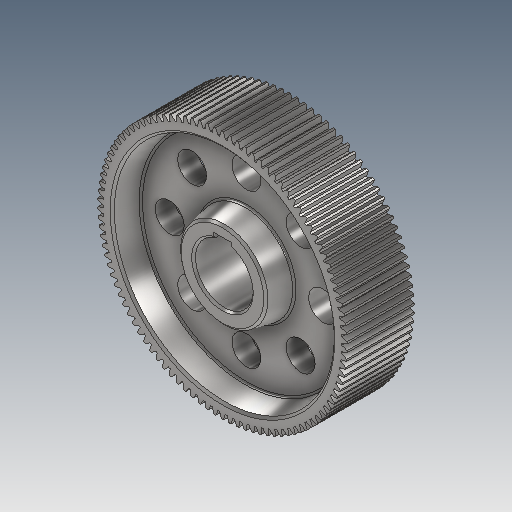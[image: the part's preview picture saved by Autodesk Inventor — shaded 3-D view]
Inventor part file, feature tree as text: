
AUTODESK INVENTOR PART (.ipt)
format: ipt  version: 2025 (Build 290162000, 162)  size: 814,592 bytes
history: native  units: mm (DEFAULTED — no unit token found)
features: sketch x5, extrude x4, plane x3, other x3, mirror x1, chamfer x1, fillet x1
ambient origin geometry x8: Origin, YZ Plane, XZ Plane, XY Plane, X Axis, Y Axis, Z Axis, Center Point
bodies: Solid1 (feature_tree)
feature tree (18):
  extrude  "Extrusion1"  Depth=70.0mm TaperAngle=0.0deg
  plane  "Work Plane2"
  plane  "Work Plane8"
  plane  "Work Plane9"
  other  "正齿轮"
  extrude  "拉伸2"  Depth=10.0mm TaperAngle=0.0deg
  extrude  "拉伸3"  Depth=0.307999mm TaperAngle=0.0deg
  mirror  "镜像1"
  extrude  "拉伸4"  TaperAngle=0.0deg  [1 undecoded]
  chamfer  "倒角1"  Distance=166.25mm
  other  "轮毂键槽"
  fillet  "圆角1"  [1 undecoded]
  sketch  "Sketch1"  dims[d0=260.0mm d1=70.0mm d2=0.0mm]
  other  "Srf1"
  sketch  "草图3"  dims[d16=166.25mm d17=0.0mm d34=0.307999mm]
  sketch  "草图4"  dims[d39=0.0mm d41=0.0mm]
  sketch  "草图5"  dims[d43=166.25mm d46=166.25mm d47=0.0mm d48=0.0mm d49=60.0mm d50=18.0mm d51=11.0mm d52=18.0mm d53=0.0mm d54=90.0mm d55=230.0mm d56=25.0mm d57=-2.007129mm d58=30.0mm d60=80.0mm d62=360.0deg d64=70.0mm d65=0.0mm d66=2.0mm d67=2.0mm d68=45.0deg d69=2.0mm d70=160.0mm]
  sketch  "草图 - 环形阵列1"  dims[d3=255.0mm d4=10.0mm d5=0.0mm]
note: 2 required parameter values undecoded (feature->parameter linkage not recoverable at this tier; creation-order binding heuristic only, values carry confidence <= 0.55)
